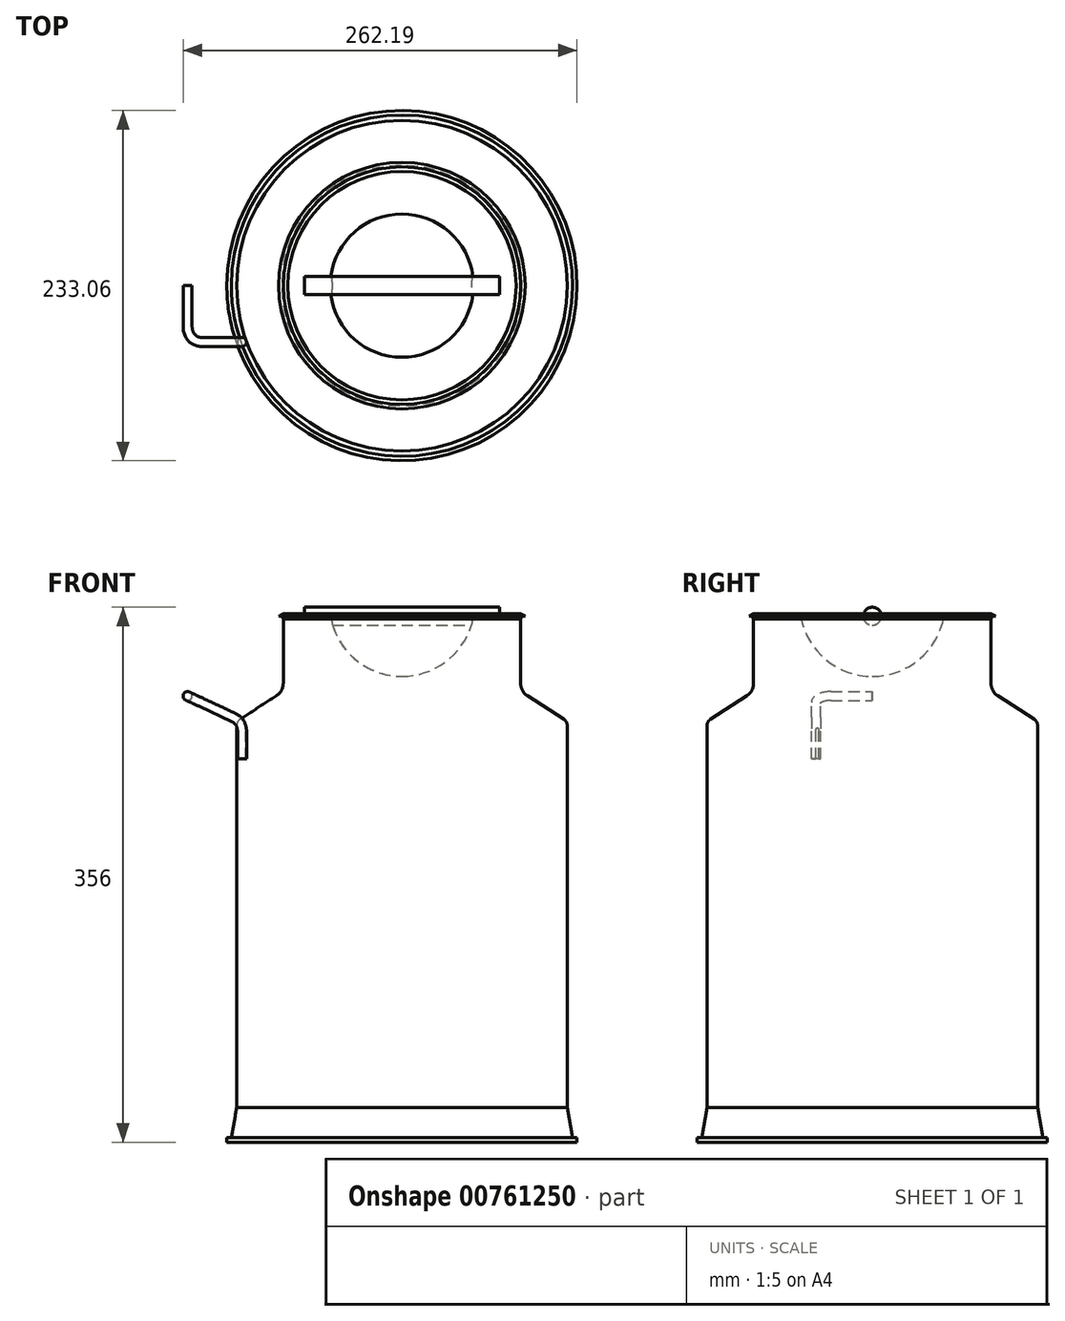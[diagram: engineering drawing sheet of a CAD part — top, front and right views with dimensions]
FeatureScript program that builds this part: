
annotation { "Feature Type Name" : "Feature", "Feature Type Description" : "" }
export const myFeature = defineFeature(function(context is Context, id is Id, definition is map)
    precondition{}
    {
        {
            var Q0;
            Q0=qCreatedBy(makeId("Front.planeOp"),FACE);
            var sketch = newSketch(context, id + "F0", { "sketchPlane" : qUnion([Q0])});
            skLineSegment(sketch, "E0", {"start": v(0, -166.73) * mm, "end": v(0, 580.86) * mm, "construction": true});
            skLineSegment(sketch, "E1", {"start": v(0, 0) * mm, "end": v(-116.53, 0) * mm});
            skLineSegment(sketch, "E2", {"start": v(-110, 23) * mm, "end": v(-110, 277.28) * mm});
            skLineSegment(sketch, "E3", {"start": v(-107.71, 281.48) * mm, "end": v(-83.58, 297.05) * mm});
            skLineSegment(sketch, "E4", {"start": v(-79, 305.45) * mm, "end": v(-79, 348.27) * mm});
            skLineSegment(sketch, "E5", {"start": v(-76, 350) * mm, "end": v(-47.67, 350) * mm});
            skLineSegment(sketch, "E6", {"start": v(0, 310) * mm, "end": v(0, 0) * mm});
            skPoint(sketch, "E7.visualSharp", {"position": v(-79, 300) * mm});
            skArc(sketch, "E7.filletArc", {"start": v(-83.58, 297.05) * mm, "mid": v(-80.22, 300.66) * mm, "end": v(-79, 305.45) * mm});
            skPoint(sketch, "E8.visualSharp", {"position": v(-110, 280) * mm});
            skArc(sketch, "E8.filletArc", {"start": v(-107.71, 281.48) * mm, "mid": v(-109.4, 279.67) * mm, "end": v(-110, 277.28) * mm});
            skArc(sketch, "E9", {"start": v(-47.67, 350) * mm, "mid": v(-31.11, 321.32) * mm, "end": v(0, 310) * mm});
            skLineSegment(sketch, "E10", {"start": v(0, 310) * mm, "end": v(31.19, 310) * mm, "construction": true});
            skLineSegment(sketch, "E11", {"start": v(-47.67, 350) * mm, "end": v(-49.64, 361.2) * mm, "construction": true});
            skPoint(sketch, "E12.orphan", {"position": v(0, 350) * mm});
            skLineSegment(sketch, "E13", {"start": v(-79, 348.27) * mm, "end": v(-80, 350) * mm});
            skLineSegment(sketch, "E14", {"start": v(-80, 350) * mm, "end": v(-82, 350) * mm});
            skLineSegment(sketch, "E15", {"start": v(-82, 350) * mm, "end": v(-79, 351.73) * mm});
            skLineSegment(sketch, "E16", {"start": v(-79, 351.73) * mm, "end": v(-76, 350) * mm});
            skPoint(sketch, "E17.orphan", {"position": v(-79, 350) * mm});
            skLineSegment(sketch, "E18", {"start": v(-110, 23) * mm, "end": v(-113.53, 3) * mm});
            skLineSegment(sketch, "E19", {"start": v(-113.53, 3) * mm, "end": v(-116.53, 3) * mm});
            skLineSegment(sketch, "E20", {"start": v(-116.53, 3) * mm, "end": v(-116.53, 0) * mm});
            skSolve(sketch);
        }
        {
            var Q0;
            Q0 = qSketchRegion(id + "F0", true);
            var Q1;
            Q1=sQuery(id+"F0.wireOp",EDGE,"E0");
            revolve(context, id + "F1", {"surfaceOperationType" : NewSurfaceOperationType.NEW, "entities" : qUnion([Q0]), "axis" : qUnion([Q1]), "revolveType" : RevolveType.FULL});
        }
        {
            var Q0;
            Q0=qCreatedBy(makeId("Front.planeOp"),FACE);
            cPlane(context, id + "F2", {"entities" : qUnion([Q0]), "cplaneType" : CPlaneType.OFFSET, "offset" : (75 / 2) * mm, "width" : 150 * mm, "height" : 150 * mm});
        }
        {
            var Q0;
            Q0=qCreatedBy(id+"F2.planeOp",FACE);
            var sketch = newSketch(context, id + "F3", { "sketchPlane" : qUnion([Q0])});
            skLineSegment(sketch, "E21", {"start": v(-106.41, 255) * mm, "end": v(-106.41, 273.63) * mm});
            skLineSegment(sketch, "E22", {"start": v(-112.18, 282.7) * mm, "end": v(-133.6, 292.68) * mm});
            skPoint(sketch, "E23.visualSharp", {"position": v(-106.41, 280) * mm});
            skArc(sketch, "E23.filletArc", {"start": v(-106.41, 273.63) * mm, "mid": v(-107.98, 279) * mm, "end": v(-112.18, 282.7) * mm});
            skLineSegment(sketch, "E24", {"start": v(-112.18, 282.7) * mm, "end": v(-96.8, 315.68) * mm, "construction": true});
            skLineSegment(sketch, "E25", {"start": v(-103.41, 277.28) * mm, "end": v(-103.41, 0) * mm, "construction": true});
            skSolve(sketch);
        }
        {
            var Q0;
            Q0=sQuery(id+"F3.wireOp",VERTEX,"E22.start");
            var Q1;
            Q1=sQuery(id+"F3.wireOp",EDGE,"E24");
            cPlane(context, id + "F4", {"entities" : qUnion([Q0, Q1]), "cplaneType" : CPlaneType.LINE_POINT, "offset" : 25 * mm, "width" : 150 * mm, "height" : 150 * mm});
        }
        {
            var Q0;
            Q0=qCreatedBy(id+"F4.planeOp",FACE);
            var sketch = newSketch(context, id + "F5", { "sketchPlane" : qUnion([Q0])});
            skArc(sketch, "E26", {"start": v(-254.77, -27.5) * mm, "mid": v(-251.84, -34.57) * mm, "end": v(-244.77, -37.5) * mm});
            skLineSegment(sketch, "E27", {"start": v(-254.77, -27.5) * mm, "end": v(-254.77, 0) * mm});
            skSolve(sketch);
        }
        {
            var Q0;
            Q0=sQuery(id+"F3.wireOp",EDGE,"E21");
            var Q1;
            Q1=sQuery(id+"F3.wireOp",VERTEX,"E21.start");
            cPlane(context, id + "F6", {"entities" : qUnion([Q0, Q1]), "cplaneType" : CPlaneType.LINE_POINT, "offset" : 25 * mm, "width" : 150 * mm, "height" : 150 * mm});
        }
        {
            var Q0;
            Q0=qCreatedBy(id+"F6.planeOp",FACE);
            var sketch = newSketch(context, id + "F7", { "sketchPlane" : qUnion([Q0])});
            skCircle(sketch, "E28", {"center": v(-106.41, -37.5) * mm, "radius": 3 * mm});
            skSolve(sketch);
        }
        {
            var Q0;
            Q0=makeQuery(id+"F7.imprint","IMPRINT",FACE,{"disambiguationData":[TD([[makeQuery(id+"F7.imprint","IMPRINT",EDGE,{"derivedFrom":sQuery(id+"F7.wireOp",EDGE,"E28")}),1.0]])]});
            var Q1;
            Q1=sQuery(id+"F3.wireOp",EDGE,"E21");
            var Q2;
            Q2=sQuery(id+"F3.wireOp",EDGE,"E23.filletArc");
            var Q3;
            Q3=sQuery(id+"F3.wireOp",EDGE,"E22");
            var Q4;
            Q4=sQuery(id+"F5.wireOp",EDGE,"E26");
            var Q5;
            Q5=sQuery(id+"F5.wireOp",EDGE,"E27");
            sweep(context, id + "F8", {"operationType" : NewBodyOperationType.ADD, "profiles" : qUnion([Q0]), "path" : qUnion([Q1, Q2, Q3, Q4, Q5])});
        }
        {
            var Q0;
            Q0=qCreatedBy(makeId("Right.planeOp"),FACE);
            var sketch = newSketch(context, id + "F9", { "sketchPlane" : qUnion([Q0])});
            skCircle(sketch, "E29", {"center": v(0, 350) * mm, "radius": 6 * mm});
            skSolve(sketch);
        }
        {
            var Q0;
            Q0 = qSketchRegion(id + "F9", true);
            extrude(context, id + "F10", {"entities" : qUnion([Q0]), "operationType" : NewBodyOperationType.ADD, "oppositeDirection" : true, "depth" : 130 * mm, "offsetDistance" : 25 * mm, "symmetric" : true});
        }
    });
